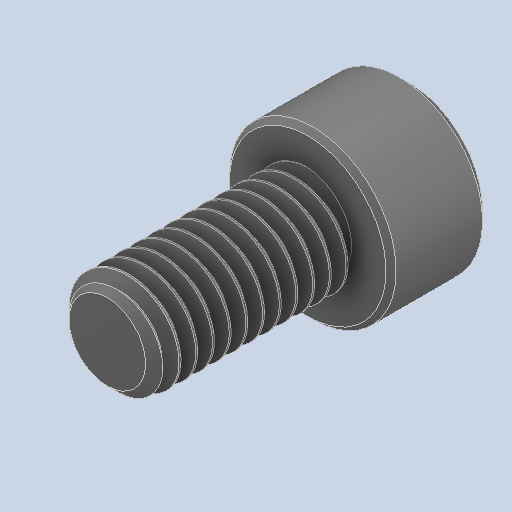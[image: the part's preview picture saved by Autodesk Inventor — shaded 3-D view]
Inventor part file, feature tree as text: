
AUTODESK INVENTOR PART (.ipt)
format: ipt  version: 2024.2 (Build 282272000, 272)  size: 523,264 bytes
history: native  units: in
note: dims shown in document units (in); Inventor stores cm internally (conversion verified against a paired STEP export)
features: chamfer x1
ambient origin geometry x8: Origin, YZ Plane, XZ Plane, XY Plane, X Axis, Y Axis, Z Axis, Center Point
bodies: Solid1 (feature_tree)
feature tree (1):
  chamfer  "Chamfer2"  [1 undecoded]
note: 1 required parameter value undecoded (feature->parameter linkage not recoverable at this tier; creation-order binding heuristic only, values carry confidence <= 0.55)
